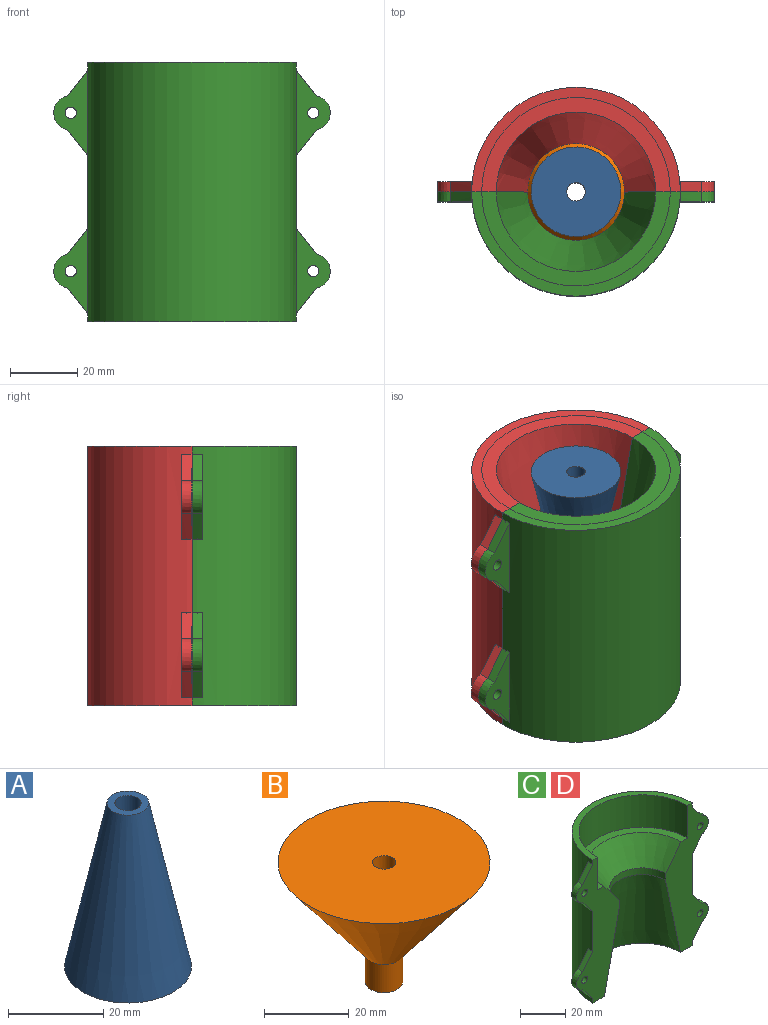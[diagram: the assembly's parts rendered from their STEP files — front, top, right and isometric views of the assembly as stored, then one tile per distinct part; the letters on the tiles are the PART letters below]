
ASSEMBLY  parts=4 mates=3
PART A: 4 faces, bbox 26.6x26.6x41.9 mm
  f0: plane 8.8x8.8mm, normal (0,0,1), area 37mm2, adj f1,f3
  f1: cone r=13.31mm half-angle=12deg, axis (0,0,-1), area 2384.6mm2, adj f0,f2
  f2: plane 26.62x26.62mm, normal (0,0,-1), area 532.8mm2, adj f1,f3
  f3: cylinder r=2.75mm len=41.93mm, axis (0,0,1), area 724.5mm2, adj f0,f2
PART B: 5 faces, bbox 50x50x34.5 mm
  f0: cylinder r=4.4mm len=8.8mm, axis (0,0,1), area 224.8mm2, adj f1,f4
  f1: cone r=4.4mm half-angle=38deg, axis (0,0,1), area 3084.6mm2, adj f0,f2
  f2: plane 49.95x49.95mm, normal (0,0,1), area 1936.1mm2, adj f1,f3
  f3: cylinder r=2.75mm len=34.48mm, axis (0,0,1), area 595.7mm2, adj f2,f4
  f4: plane 8.8x8.8mm, normal (0,0,-1), area 37mm2, adj f0,f3
PART C: 35 faces, bbox 82.6x31.6x77.5 mm
  f0: cylinder r=28mm len=56mm, axis (0,0,1), area 1538.8mm2, adj f2,f3,f5,f30
  f1: cylinder r=31mm len=77mm, axis (0,0,1), area 7345.4mm2, adj f2,f3,f4,f5,f6,f10,f14,f18
  f2: plane 77.02x26.62mm, normal (0,-1,0), area 1031.7mm2, adj f0,f1,f4,f5,f11,f12,f19,f20
  f3: plane 77.02x26.62mm, normal (0,-1,0), area 1031.6mm2, adj f0,f1,f4,f5,f7,f8,f15,f16
  f4: plane 62.01x31.01mm, normal (0,0,-1), area 278.1mm2, adj f1,f2,f3,f32
  f5: plane 62x31mm, normal (0,0,1), area 278mm2, adj f0,f1,f2,f3
  f6: plane 25.77x1.83mm, normal (1,-0.02,0), area 37.8mm2, adj f1,f9,f25,f26
  f7: cone r=5mm half-angle=1.4deg, axis (0,1,0), area 40.6mm2, adj f3,f9,f25,f26
  f8: cone r=1.75mm half-angle=1.4deg, axis (0,-1,0), area 32.3mm2, adj f3,f9
  f9: plane 25.9x10.64mm, normal (0,1,0), area 129.8mm2, adj f6,f7,f8,f25,f26
  f10: plane 25.77x1.83mm, normal (-1,-0.02,0), area 37.8mm2, adj f1,f13,f24,f29
  f11: cone r=5mm half-angle=1.4deg, axis (0,1,0), area 40.6mm2, adj f2,f13,f24,f29
  f12: cone r=1.75mm half-angle=1.4deg, axis (0,-1,0), area 32.3mm2, adj f2,f13
  f13: plane 25.9x10.64mm, normal (0,1,0), area 129.8mm2, adj f10,f11,f12,f24,f29
  f14: plane 25.77x1.83mm, normal (1,-0.02,0), area 37.8mm2, adj f1,f17,f22,f27
  f15: cone r=5mm half-angle=1.4deg, axis (0,1,0), area 40.6mm2, adj f3,f17,f22,f27
  f16: cone r=1.75mm half-angle=1.4deg, axis (0,-1,0), area 32.3mm2, adj f3,f17
  f17: plane 25.9x10.64mm, normal (0,1,0), area 129.8mm2, adj f14,f15,f16,f22,f27
  f18: plane 25.77x1.83mm, normal (-1,-0.02,0), area 37.8mm2, adj f1,f21,f23,f28
  f19: cone r=1.75mm half-angle=1.4deg, axis (0,-1,0), area 32.3mm2, adj f2,f21
  f20: cone r=5mm half-angle=1.4deg, axis (0,1,0), area 40.6mm2, adj f2,f21,f23,f28
  f21: plane 25.9x10.64mm, normal (0,1,0), area 129.8mm2, adj f18,f19,f20,f23,f28
  f22: bspline ~7.92x6.29mm, area 30.1mm2, adj f1,f3,f14,f15,f17
  f23: bspline ~7.92x6.29mm, area 30.1mm2, adj f1,f2,f18,f20,f21
  f24: bspline ~7.92x6.29mm, area 30.1mm2, adj f1,f2,f10,f11,f13
  f25: bspline ~7.92x6.29mm, area 30.1mm2, adj f1,f3,f6,f7,f9
  f26: bspline ~7.92x6.29mm, area 30.1mm2, adj f1,f3,f6,f7,f9
  f27: bspline ~7.92x6.29mm, area 30.1mm2, adj f1,f3,f14,f15,f17
  f28: bspline ~7.92x6.29mm, area 30.1mm2, adj f1,f2,f18,f20,f21
  f29: bspline ~7.92x6.29mm, area 30.1mm2, adj f1,f2,f10,f11,f13
  f30: plane 56x28mm, normal (0,0,1), area 326.7mm2, adj f0,f2,f3,f33
  f31: cone r=23.66mm half-angle=12deg, axis (0,0,-1), area 2663.5mm2, adj f2,f3,f32,f34
  f32: plane 56.01x28.01mm, normal (0,0,-1), area 352.1mm2, adj f2,f3,f4,f31
  f33: cone r=14.4mm half-angle=38deg, axis (0,0,1), area 940.7mm2, adj f2,f3,f30,f34
  f34: cylinder r=14.4mm len=28.8mm, axis (0,0,1), area 164.7mm2, adj f2,f3,f31,f33
PART D: same geometry as C
PLACE A rot(axis=(0,1,0),180deg) t=(0,0,76.4)mm
PLACE B rot(axis=(0,1,0),180deg) t=(0,0,76.4)mm
PLACE C rot(axis=(-1,0,0),180deg) t=(0,0,76.4)mm
PLACE D rot(axis=(0,1,0),180deg) t=(0,0,76.4)mm
MATE fastened B.f0 <-> D.f0  axis (0,0,-1) through (0,0,0)mm
MATE parallel B.f3 <-> A.f3  axis (0,0,1) through (0,0,34.48)mm
MATE fastened C.f0 <-> B.f0  axis (0,0,-1) through (0,0,0)mm
